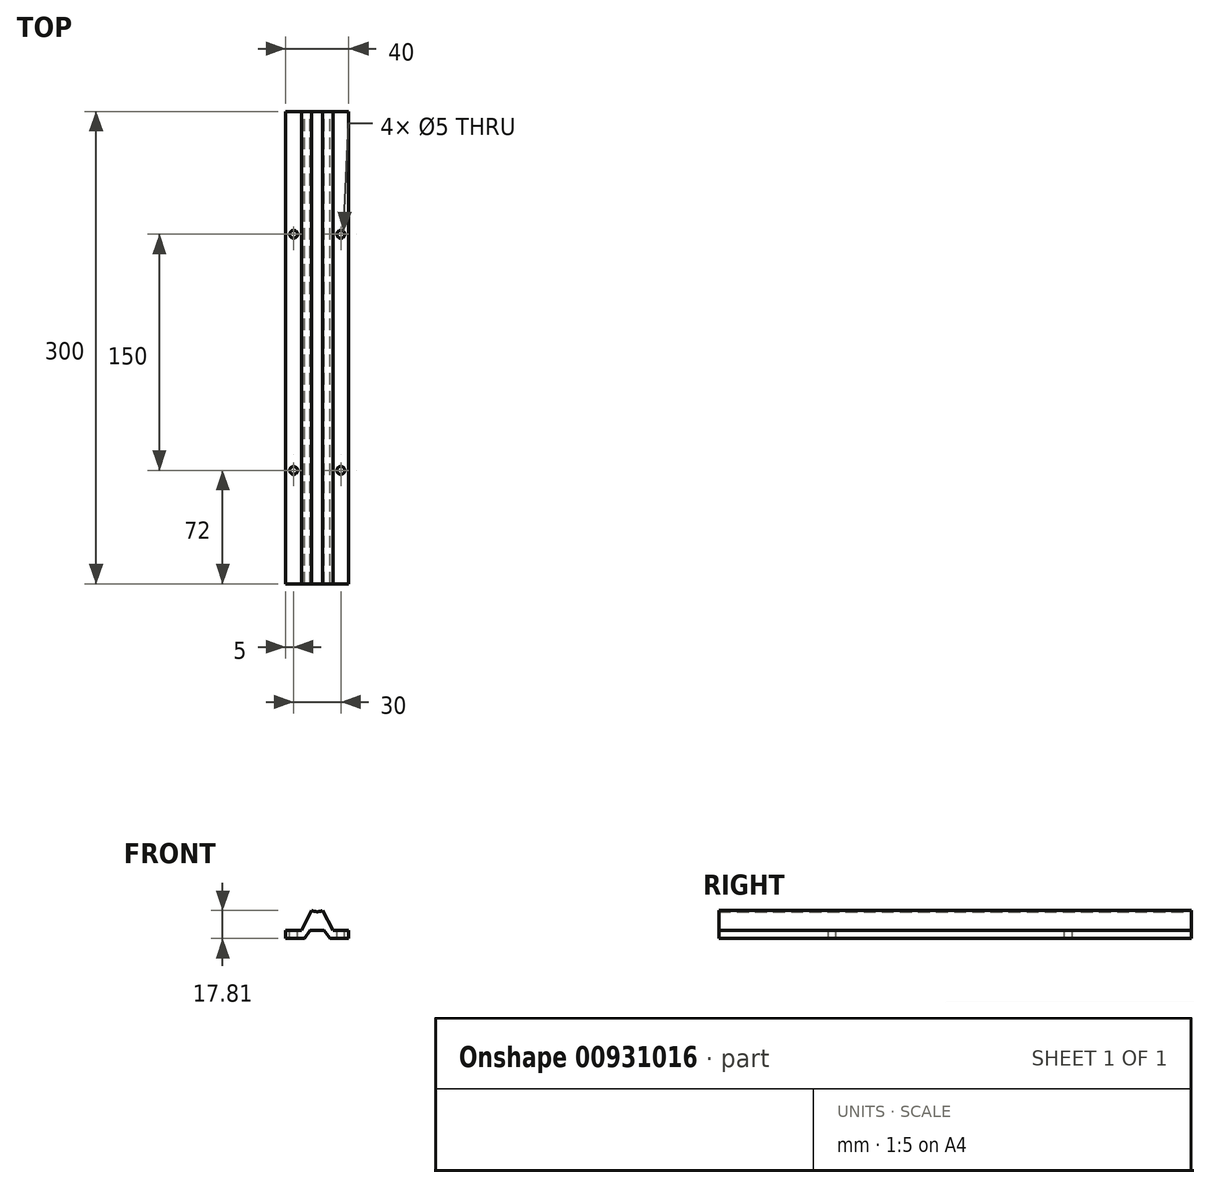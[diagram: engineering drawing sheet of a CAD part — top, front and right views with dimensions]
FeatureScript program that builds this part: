
annotation { "Feature Type Name" : "Feature", "Feature Type Description" : "" }
export const myFeature = defineFeature(function(context is Context, id is Id, definition is map)
    precondition{}
    {
        {
            var Q0;
            Q0=qCreatedBy(makeId("Front.planeOp"),FACE);
            var sketch = newSketch(context, id + "F0", { "sketchPlane" : qUnion([Q0])});
            skCircle(sketch, "E0", {"center": v(0, 0) * mm, "radius": 8 * mm, "construction": true});
            skLineSegment(sketch, "E1", {"start": v(0, 8) * mm, "end": v(0, -8) * mm, "construction": true});
            skLineSegment(sketch, "E2", {"start": v(0, -7.2) * mm, "end": v(3.5, -7.2) * mm, "construction": true});
            skLineSegment(sketch, "E3", {"start": v(0, -8) * mm, "end": v(0, -20) * mm, "construction": true});
            skLineSegment(sketch, "E4", {"start": v(0, -20) * mm, "end": v(4.5, -20) * mm});
            skLineSegment(sketch, "E5", {"start": v(0, -20) * mm, "end": v(0, -25) * mm, "construction": true});
            skLineSegment(sketch, "E6", {"start": v(0, -25) * mm, "end": v(8, -25) * mm, "construction": true});
            skLineSegment(sketch, "E7", {"start": v(4.5, -20) * mm, "end": v(8, -25) * mm});
            skLineSegment(sketch, "E8", {"start": v(8, -25) * mm, "end": v(20, -25) * mm});
            skLineSegment(sketch, "E9", {"start": v(20, -25) * mm, "end": v(20, -20) * mm});
            skLineSegment(sketch, "E10", {"start": v(20, -20) * mm, "end": v(10, -20) * mm});
            skLineSegment(sketch, "E11", {"start": v(10, -20) * mm, "end": v(3.5, -7.2) * mm});
            skArc(sketch, "E12", {"start": v(0, -8) * mm, "mid": v(1.8, -7.8) * mm, "end": v(3.5, -7.2) * mm});
            skLineSegment(sketch, "E13.MirrorCS", {"start": v(-10, -20) * mm, "end": v(-3.5, -7.2) * mm});
            skLineSegment(sketch, "E14.MirrorCS", {"start": v(-20, -20) * mm, "end": v(-10, -20) * mm});
            skLineSegment(sketch, "E15.MirrorCS", {"start": v(-20, -25) * mm, "end": v(-20, -20) * mm});
            skLineSegment(sketch, "E16.MirrorCS", {"start": v(-8, -25) * mm, "end": v(-20, -25) * mm});
            skLineSegment(sketch, "E17.MirrorCS", {"start": v(-4.5, -20) * mm, "end": v(-8, -25) * mm});
            skLineSegment(sketch, "E18.MirrorCS", {"start": v(0, -20) * mm, "end": v(-4.5, -20) * mm});
            skArc(sketch, "E19.MirrorCS", {"start": v(0, -8) * mm, "mid": v(-1.8, -7.8) * mm, "end": v(-3.5, -7.2) * mm});
            skSolve(sketch);
        }
        {
            var Q0;
            Q0 = qSketchRegion(id + "F0", true);
            extrude(context, id + "F1", {"entities" : qUnion([Q0]), "depth" : 300 * mm, "offsetDistance" : 25 * mm});
        }
        {
            var Q0;
            Q0=makeQuery(id+"F1.opExtrude","SWEPT_FACE",FACE,{"disambiguationData":[OSD([sQuery(id+"F0.wireOp",EDGE,"E10")])]});
            var sketch = newSketch(context, id + "F2", { "sketchPlane" : qUnion([Q0])});
            skCircle(sketch, "E20", {"center": v(15, -228) * mm, "radius": 2.5 * mm});
            skCircle(sketch, "E21", {"center": v(15, -78) * mm, "radius": 2.5 * mm});
            skCircle(sketch, "E22.MirrorC", {"center": v(-15, -78) * mm, "radius": 2.5 * mm});
            skCircle(sketch, "E23.MirrorC", {"center": v(-15, -228) * mm, "radius": 2.5 * mm});
            skSolve(sketch);
        }
        {
            var Q0;
            Q0 = qSketchRegion(id + "F2", true);
            var Q1;
            Q1=makeQuery(id+"F1.opExtrude","SWEPT_FACE",FACE,{"disambiguationData":[OSD([sQuery(id+"F0.wireOp",EDGE,"E8")])]});
            extrude(context, id + "F3", {"entities" : qUnion([Q0]), "operationType" : NewBodyOperationType.REMOVE, "endBound" : BoundingType.UP_TO_SURFACE, "oppositeDirection" : true, "depth" : 5 * mm, "endBoundEntityFace" : qUnion([Q1]), "offsetDistance" : 25 * mm});
        }
    });
